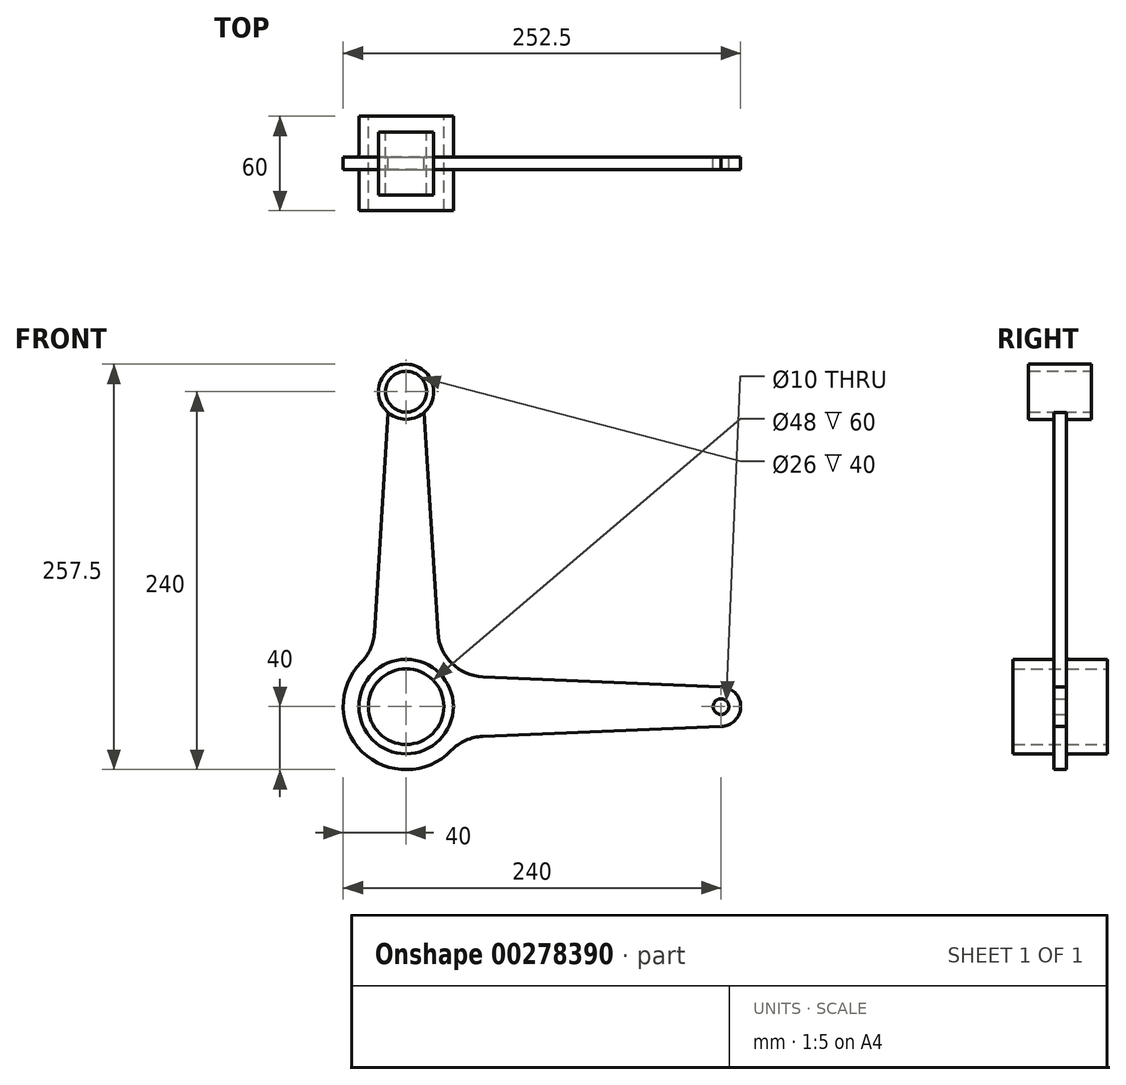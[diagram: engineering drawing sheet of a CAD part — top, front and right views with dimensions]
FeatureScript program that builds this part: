
annotation { "Feature Type Name" : "Feature", "Feature Type Description" : "" }
export const myFeature = defineFeature(function(context is Context, id is Id, definition is map)
    precondition{}
    {
        {
            var Q0;
            Q0=qCreatedBy(makeId("Front.planeOp"),FACE);
            var sketch = newSketch(context, id + "F0", { "sketchPlane" : qUnion([Q0])});
            skArc(sketch, "E0", {"start": v(-28.65, 27.91) * mm, "mid": v(-27.92, -28.64) * mm, "end": v(28.63, -27.93) * mm});
            skCircle(sketch, "E1", {"center": v(0, 200) * mm, "radius": 13 * mm});
            skCircle(sketch, "E2", {"center": v(0, 200) * mm, "radius": 17.5 * mm});
            skCircle(sketch, "E3", {"center": v(200, 0) * mm, "radius": 5 * mm});
            skArc(sketch, "E4", {"start": v(200, -12.5) * mm, "mid": v(212.5, 0) * mm, "end": v(200, 12.5) * mm});
            skLineSegment(sketch, "E5", {"start": v(20.2, 47.02) * mm, "end": v(11.5, 186.8) * mm});
            skLineSegment(sketch, "E6", {"start": v(-11.5, 186.8) * mm, "end": v(-20.2, 46.99) * mm});
            skLineSegment(sketch, "E7", {"start": v(48.86, 18.9) * mm, "end": v(200, 12.5) * mm});
            skLineSegment(sketch, "E8", {"start": v(200, -12.5) * mm, "end": v(48.83, -18.91) * mm});
            skPoint(sketch, "E9.newPointA", {"position": v(34.92, 19.5) * mm});
            skPoint(sketch, "E9.newPointB", {"position": v(21, 34.04) * mm});
            skArc(sketch, "E9.filletArc", {"start": v(20.2, 47.02) * mm, "mid": v(29.13, 27.46) * mm, "end": v(48.86, 18.9) * mm});
            skPoint(sketch, "E10.visualSharp", {"position": v(-21, 34.04) * mm});
            skArc(sketch, "E10.filletArc", {"start": v(-28.65, 27.91) * mm, "mid": v(-22.71, 36.7) * mm, "end": v(-20.2, 46.99) * mm});
            skPoint(sketch, "E11.visualSharp", {"position": v(34.92, -19.5) * mm});
            skArc(sketch, "E11.filletArc", {"start": v(48.83, -18.91) * mm, "mid": v(37.87, -21.5) * mm, "end": v(28.63, -27.93) * mm});
            skCircle(sketch, "E12", {"center": v(0, 0) * mm, "radius": 30 * mm});
            skCircle(sketch, "E13", {"center": v(0, 0) * mm, "radius": 24 * mm});
            skSolve(sketch);
        }
        {
            var Q0;
            Q0=makeQuery(id+"F0.imprint","IMPRINT",FACE,{"disambiguationData":[TD([[makeQuery(id+"F0.imprint","IMPRINT",EDGE,{"derivedFrom":sQuery(id+"F0.wireOp",EDGE,"E0")}),1.0]])]});
            extrude(context, id + "F1", {"entities" : qUnion([Q0]), "endBound" : BoundingType.SYMMETRIC, "depth" : 8 * mm});
        }
        {
            var Q0;
            Q0=makeQuery(id+"F0.imprint","IMPRINT",FACE,{"disambiguationData":[TD([[makeQuery(id+"F0.imprint","IMPRINT",EDGE,{"derivedFrom":sQuery(id+"F0.wireOp",EDGE,"E12")}),1.0]])]});
            extrude(context, id + "F2", {"entities" : qUnion([Q0]), "operationType" : NewBodyOperationType.ADD, "endBound" : BoundingType.SYMMETRIC, "depth" : 60 * mm});
        }
        {
            var Q0;
            Q0=makeQuery(id+"F0.imprint","IMPRINT",FACE,{"disambiguationData":[TD([[makeQuery(id+"F0.imprint","IMPRINT",EDGE,{"derivedFrom":sQuery(id+"F0.wireOp",EDGE,"E1")}),-1.0]])]});
            extrude(context, id + "F3", {"entities" : qUnion([Q0]), "operationType" : NewBodyOperationType.ADD, "endBound" : BoundingType.SYMMETRIC, "depth" : 40 * mm});
        }
        {
            var Q0;
            Q0=makeQuery(id+"F1.opExtrude","CAP_EDGE",EDGE,{"disambiguationData":[OSD([sQuery(id+"F0.wireOp",EDGE,"E12")])],"isStart":false});
            var Q1;
            Q1=makeQuery(id+"F1.opExtrude","CAP_EDGE",EDGE,{"disambiguationData":[OSD([sQuery(id+"F0.wireOp",EDGE,"E12")])],"isStart":true});
            var Q2;
            Q2=makeQuery(id+"F1.opExtrude","CAP_EDGE",EDGE,{"disambiguationData":[OSD([sQuery(id+"F0.wireOp",EDGE,"E2")])],"isStart":false});
            var Q3;
            Q3=makeQuery(id+"F1.opExtrude","SWEPT_EDGE",EDGE,{"disambiguationData":[OSD([sQuery(id+"F0.wireOp",EDGE,"E2"),sQuery(id+"F0.wireOp",EDGE,"E5")])]});
            var Q4;
            Q4=makeQuery(id+"F1.opExtrude","CAP_EDGE",EDGE,{"disambiguationData":[OSD([sQuery(id+"F0.wireOp",EDGE,"E2")])],"isStart":true});
            var Q5;
            Q5=makeQuery(id+"F1.opExtrude","SWEPT_EDGE",EDGE,{"disambiguationData":[OSD([sQuery(id+"F0.wireOp",EDGE,"E2"),sQuery(id+"F0.wireOp",EDGE,"E6")])]});
            fillet(context, id + "F4", {"entities" : qUnion([Q0, Q1, Q2, Q3, Q4, Q5]), "radius" : 2 * mm, "tangentPropagation" : true, "allowEdgeOverflow" : false});
        }
    });
